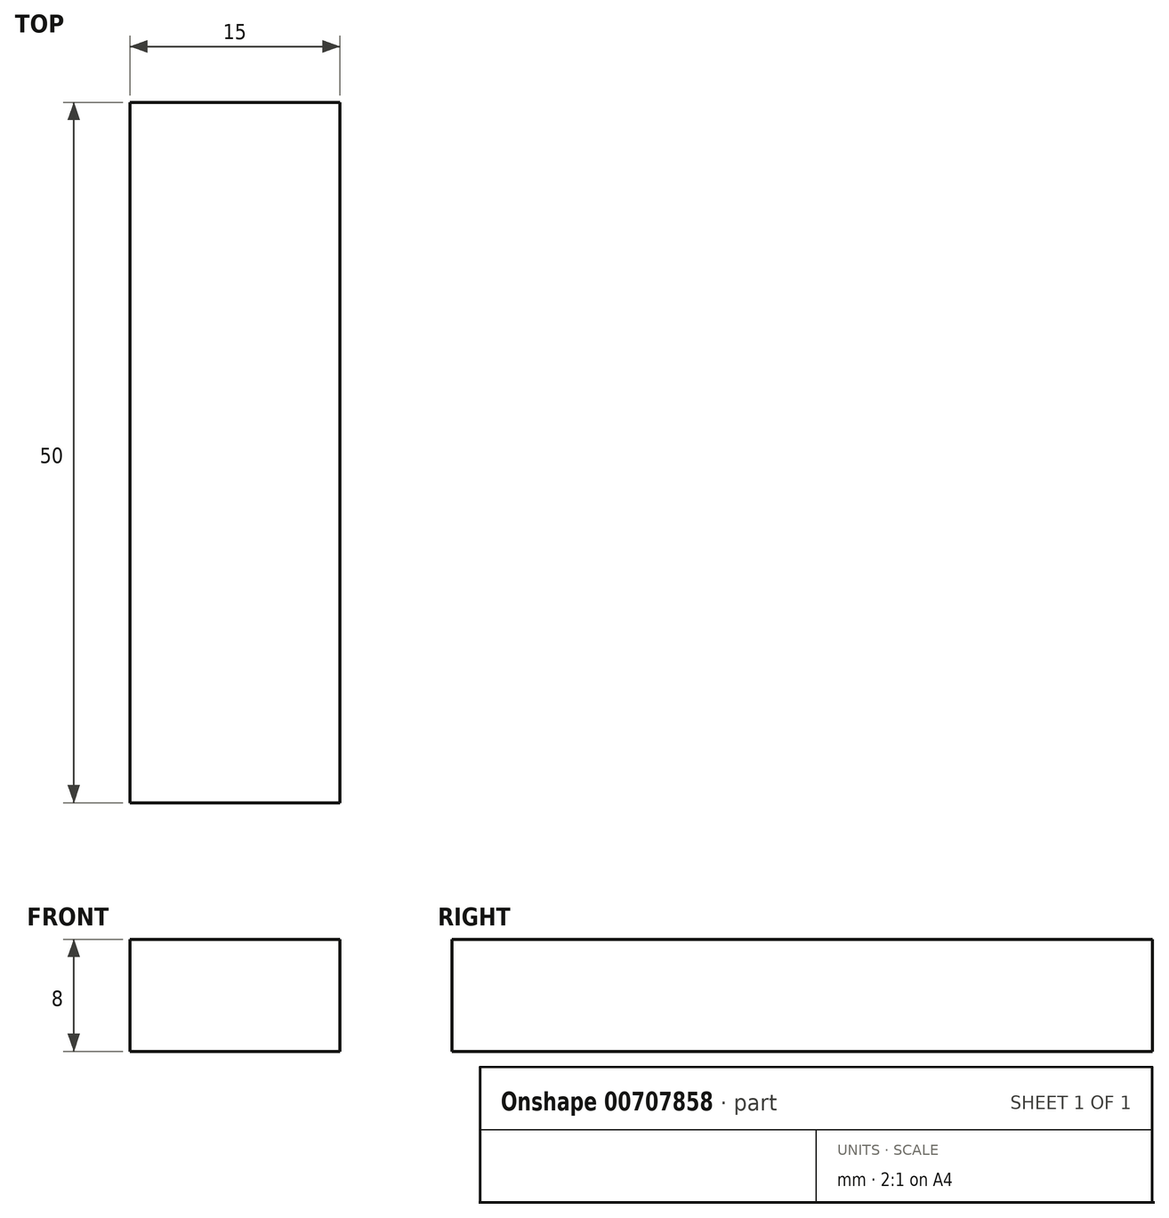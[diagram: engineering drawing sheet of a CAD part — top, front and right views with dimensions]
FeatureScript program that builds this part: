
annotation { "Feature Type Name" : "Feature", "Feature Type Description" : "" }
export const myFeature = defineFeature(function(context is Context, id is Id, definition is map)
    precondition{}
    {
        {
            var Q0;
            Q0=qCreatedBy(makeId("Top.planeOp"),FACE);
            var sketch = newSketch(context, id + "F0", { "sketchPlane" : qUnion([Q0])});
            skLineSegment(sketch, "E0.bottom", {"start": v(-30.43, 71.88) * mm, "end": v(-15.43, 71.88) * mm});
            skLineSegment(sketch, "E0.top", {"start": v(-30.43, 21.88) * mm, "end": v(-15.43, 21.88) * mm});
            skLineSegment(sketch, "E0.left", {"start": v(-30.43, 71.88) * mm, "end": v(-30.43, 21.88) * mm});
            skLineSegment(sketch, "E0.right", {"start": v(-15.43, 71.88) * mm, "end": v(-15.43, 21.88) * mm});
            skSolve(sketch);
        }
        {
            var Q0;
            Q0 = qSketchRegion(id + "F0", true);
            extrude(context, id + "F1", {"entities" : qUnion([Q0]), "depth" : 8 * mm, "offsetDistance" : 25 * mm});
        }
    });
